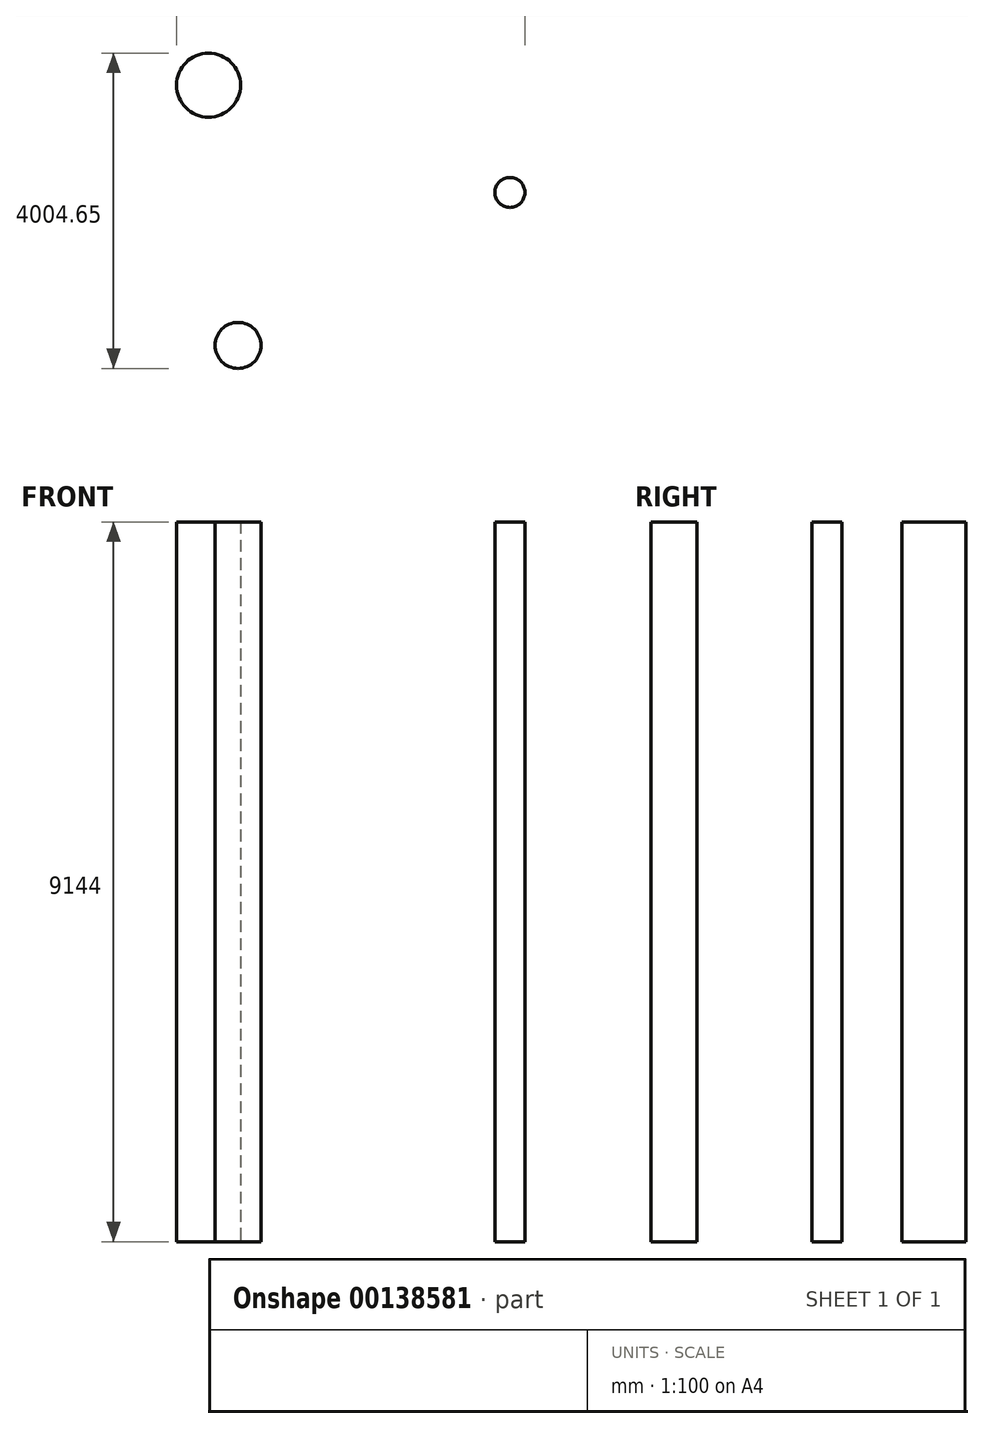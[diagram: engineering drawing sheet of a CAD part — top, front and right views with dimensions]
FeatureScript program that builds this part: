
annotation { "Feature Type Name" : "Feature", "Feature Type Description" : "" }
export const myFeature = defineFeature(function(context is Context, id is Id, definition is map)
    precondition{}
    {
        {
            var Q0;
            Q0=qCreatedBy(makeId("Top.planeOp"),FACE);
            var sketch = newSketch(context, id + "F0", { "sketchPlane" : qUnion([Q0])});
            skCircle(sketch, "E0", {"center": v(0, 0) * mm, "radius": 406.4 * mm});
            skCircle(sketch, "E1", {"center": v(375.44, -3306.15) * mm, "radius": 292.1 * mm});
            skCircle(sketch, "E2", {"center": v(3828.64, -1362.95) * mm, "radius": 190.5 * mm});
            skPoint(sketch, "E3", {"position": v(4276.12, -3598.25) * mm});
            skLineSegment(sketch, "E4", {"start": v(4276.12, -3598.25) * mm, "end": v(-6201.85, -3598.25) * mm, "construction": true});
            skSolve(sketch);
        }
        {
            var Q0;
            Q0 = qSketchRegion(id + "F0", true);
            extrude(context, id + "F1", {"entities" : qUnion([Q0]), "depth" : 9144 * mm});
        }
        {
            var Q0;
            Q0=qCreatedBy(makeId("Top.planeOp"),FACE);
            cPlane(context, id + "F2", {"entities" : qUnion([Q0]), "cplaneType" : CPlaneType.OFFSET, "offset" : 2438.4 * mm, "width" : 152.4 * mm, "height" : 152.4 * mm});
        }
    });
